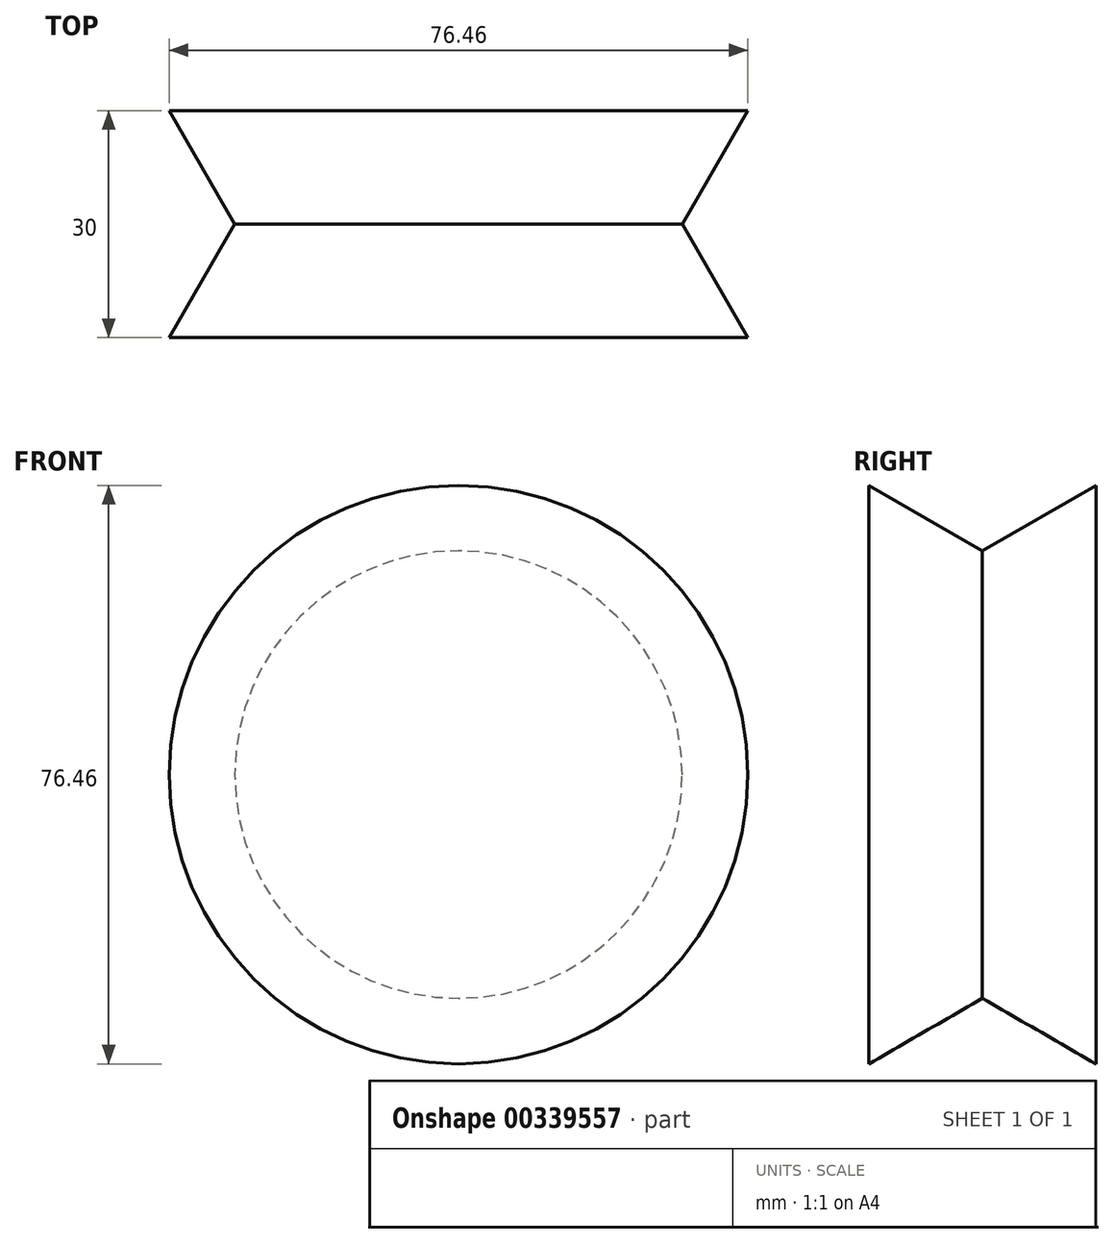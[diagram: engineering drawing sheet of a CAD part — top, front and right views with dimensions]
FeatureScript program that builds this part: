
annotation { "Feature Type Name" : "Feature", "Feature Type Description" : "" }
export const myFeature = defineFeature(function(context is Context, id is Id, definition is map)
    precondition{}
    {
        {
            var Q0;
            Q0=qCreatedBy(makeId("Front.planeOp"),FACE);
            var sketch = newSketch(context, id + "F0", { "sketchPlane" : qUnion([Q0])});
            skCircle(sketch, "E0", {"center": v(0, 0) * mm, "radius": 38.23 * mm});
            skSolve(sketch);
        }
        {
            var Q0;
            Q0 = qSketchRegion(id + "F0", true);
            extrude(context, id + "F1", {"entities" : qUnion([Q0]), "depth" : 15 * mm, "hasDraft" : true, "draftAngle" : 30 * degree, "draftPullDirection" : true});
        }
        {
            var Q0;
            Q0=makeQuery(id+"F1.opExtrude","CAP_FACE",FACE,{"disambiguationData":[OSD([sQuery(id+"F0.wireOp",EDGE,"E0")])],"isStart":false});
            extrude(context, id + "F2", {"entities" : qUnion([Q0]), "operationType" : NewBodyOperationType.ADD, "depth" : 15 * mm, "hasDraft" : true, "draftAngle" : 30 * degree});
        }
    });
